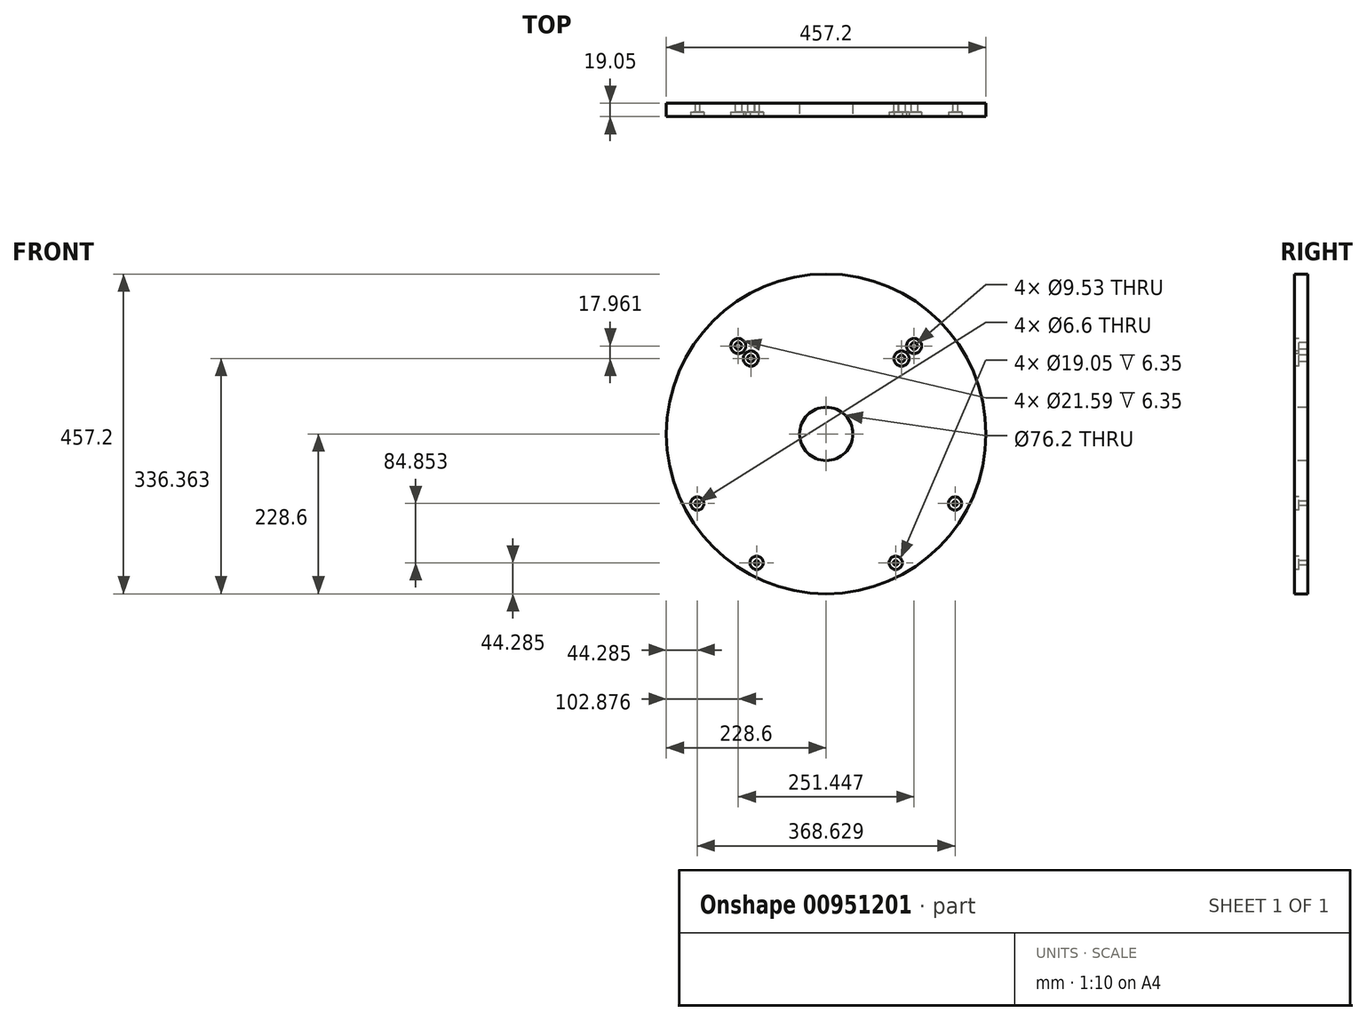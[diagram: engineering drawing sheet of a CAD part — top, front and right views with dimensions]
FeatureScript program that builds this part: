
annotation { "Feature Type Name" : "Feature", "Feature Type Description" : "" }
export const myFeature = defineFeature(function(context is Context, id is Id, definition is map)
    precondition{}
    {
        {
            var Q0;
            Q0=qCreatedBy(makeId("Front.planeOp"),FACE);
            var sketch = newSketch(context, id + "F0", { "sketchPlane" : qUnion([Q0])});
            skCircle(sketch, "E0", {"center": v(0, 0) * mm, "radius": 228.6 * mm});
            skSolve(sketch);
        }
        {
            var Q0;
            Q0=qSketchRegion(id+"F0",true);
            extrude(context, id + "F1", {"entities" : qUnion([Q0]), "depth" : 19.05 * mm, "offsetDistance" : 25.4 * mm});
        }
        {
            var Q0;
            Q0=makeQuery(id+"F1.opExtrude","CAP_FACE",FACE,{"disambiguationData":[OSD([sQuery(id+"F0.wireOp",EDGE,"E0")])],"isStart":false});
            var sketch = newSketch(context, id + "F2", { "sketchPlane" : qUnion([Q0])});
            skCircle(sketch, "E1", {"center": v(0, 0) * mm, "radius": 38.1 * mm});
            skSolve(sketch);
        }
        {
            var Q0;
            Q0=makeQuery(id+"F2.imprint","IMPRINT",FACE,{"disambiguationData":[TD([[makeQuery(id+"F2.imprint","IMPRINT",EDGE,{"derivedFrom":sQuery(id+"F2.wireOp",EDGE,"E1")}),1.0]])]});
            extrude(context, id + "F3", {"entities" : qUnion([Q0]), "operationType" : NewBodyOperationType.REMOVE, "endBound" : BoundingType.THROUGH_ALL, "oppositeDirection" : true, "depth" : 25.4 * mm, "offsetDistance" : 25.4 * mm});
        }
        {
            var Q0;
            Q0=makeQuery(id+"F1.opExtrude","CAP_FACE",FACE,{"disambiguationData":[OSD([sQuery(id+"F0.wireOp",EDGE,"E0")])],"isStart":false});
            var sketch = newSketch(context, id + "F4", { "sketchPlane" : qUnion([Q0])});
            skLineSegment(sketch, "E2", {"start": v(0, 0) * mm, "end": v(161.64, 161.64) * mm, "construction": true});
            skLineSegment(sketch, "E3", {"start": v(0, 0) * mm, "end": v(-161.64, 161.64) * mm, "construction": true});
            skLineSegment(sketch, "E4", {"start": v(-228.6, 0) * mm, "end": v(228.6, 0) * mm, "construction": true});
            skLineSegment(sketch, "E5", {"start": v(-161.64, 161.64) * mm, "end": v(-161.64, 0) * mm, "construction": true});
            skLineSegment(sketch, "E6", {"start": v(161.64, 161.64) * mm, "end": v(161.64, 0) * mm, "construction": true});
            skCircle(sketch, "E7", {"center": v(107.76, 107.76) * mm, "radius": 4.76 * mm});
            skCircle(sketch, "E8", {"center": v(125.72, 125.72) * mm, "radius": 4.76 * mm});
            skLineSegment(sketch, "E9", {"start": v(0, 0) * mm, "end": v(0, 228.6) * mm, "construction": true});
            skCircle(sketch, "E10.MirrorC", {"center": v(-107.76, 107.76) * mm, "radius": 4.76 * mm});
            skCircle(sketch, "E11.MirrorC", {"center": v(-125.72, 125.72) * mm, "radius": 4.76 * mm});
            skLineSegment(sketch, "E12", {"start": v(0, 0) * mm, "end": v(161.64, -161.64) * mm, "construction": true});
            skLineSegment(sketch, "E13", {"start": v(0, 0) * mm, "end": v(-161.64, -161.64) * mm, "construction": true});
            skLineSegment(sketch, "E14", {"start": v(0, 0) * mm, "end": v(0, -228.6) * mm, "construction": true});
            skCircle(sketch, "E15", {"center": v(-99.46, -184.31) * mm, "radius": 3.3 * mm});
            skCircle(sketch, "E16", {"center": v(-184.31, -99.46) * mm, "radius": 3.3 * mm});
            skLineSegment(sketch, "E17", {"start": v(-184.31, -99.46) * mm, "end": v(-141.89, -141.89) * mm, "construction": true});
            skLineSegment(sketch, "E18", {"start": v(-141.89, -141.89) * mm, "end": v(-99.46, -184.31) * mm, "construction": true});
            skCircle(sketch, "E19.MirrorC", {"center": v(99.46, -184.31) * mm, "radius": 3.3 * mm});
            skCircle(sketch, "E20.MirrorC", {"center": v(184.31, -99.46) * mm, "radius": 3.3 * mm});
            skSolve(sketch);
        }
        {
            var Q0;
            Q0=qSketchRegion(id+"F4",true);
            extrude(context, id + "F5", {"entities" : qUnion([Q0]), "operationType" : NewBodyOperationType.REMOVE, "endBound" : BoundingType.THROUGH_ALL, "oppositeDirection" : true, "depth" : 25.4 * mm, "offsetDistance" : 25.4 * mm});
        }
        {
            var Q0;
            Q0=makeQuery(id+"F1.opExtrude","CAP_FACE",FACE,{"disambiguationData":[OSD([sQuery(id+"F0.wireOp",EDGE,"E0")])],"isStart":false});
            var sketch = newSketch(context, id + "F6", { "sketchPlane" : qUnion([Q0])});
            skLineSegment(sketch, "E21", {"start": v(0, 0) * mm, "end": v(0, 228.6) * mm, "construction": true});
            skCircle(sketch, "E22", {"center": v(107.76, 107.76) * mm, "radius": 10.8 * mm});
            skCircle(sketch, "E23", {"center": v(125.72, 125.72) * mm, "radius": 10.8 * mm});
            skCircle(sketch, "E24.MirrorC", {"center": v(-125.72, 125.72) * mm, "radius": 10.8 * mm});
            skCircle(sketch, "E25.MirrorC", {"center": v(-107.76, 107.76) * mm, "radius": 10.8 * mm});
            skCircle(sketch, "E26", {"center": v(-184.31, -99.46) * mm, "radius": 9.53 * mm});
            skCircle(sketch, "E27", {"center": v(-99.46, -184.31) * mm, "radius": 9.53 * mm});
            skCircle(sketch, "E28", {"center": v(99.46, -184.31) * mm, "radius": 9.53 * mm});
            skCircle(sketch, "E29", {"center": v(184.31, -99.46) * mm, "radius": 9.53 * mm});
            skSolve(sketch);
        }
        {
            var Q0;
            Q0=qSketchRegion(id+"F6",true);
            extrude(context, id + "F7", {"entities" : qUnion([Q0]), "operationType" : NewBodyOperationType.REMOVE, "oppositeDirection" : true, "depth" : 6.35 * mm, "offsetDistance" : 25.4 * mm});
        }
    });
